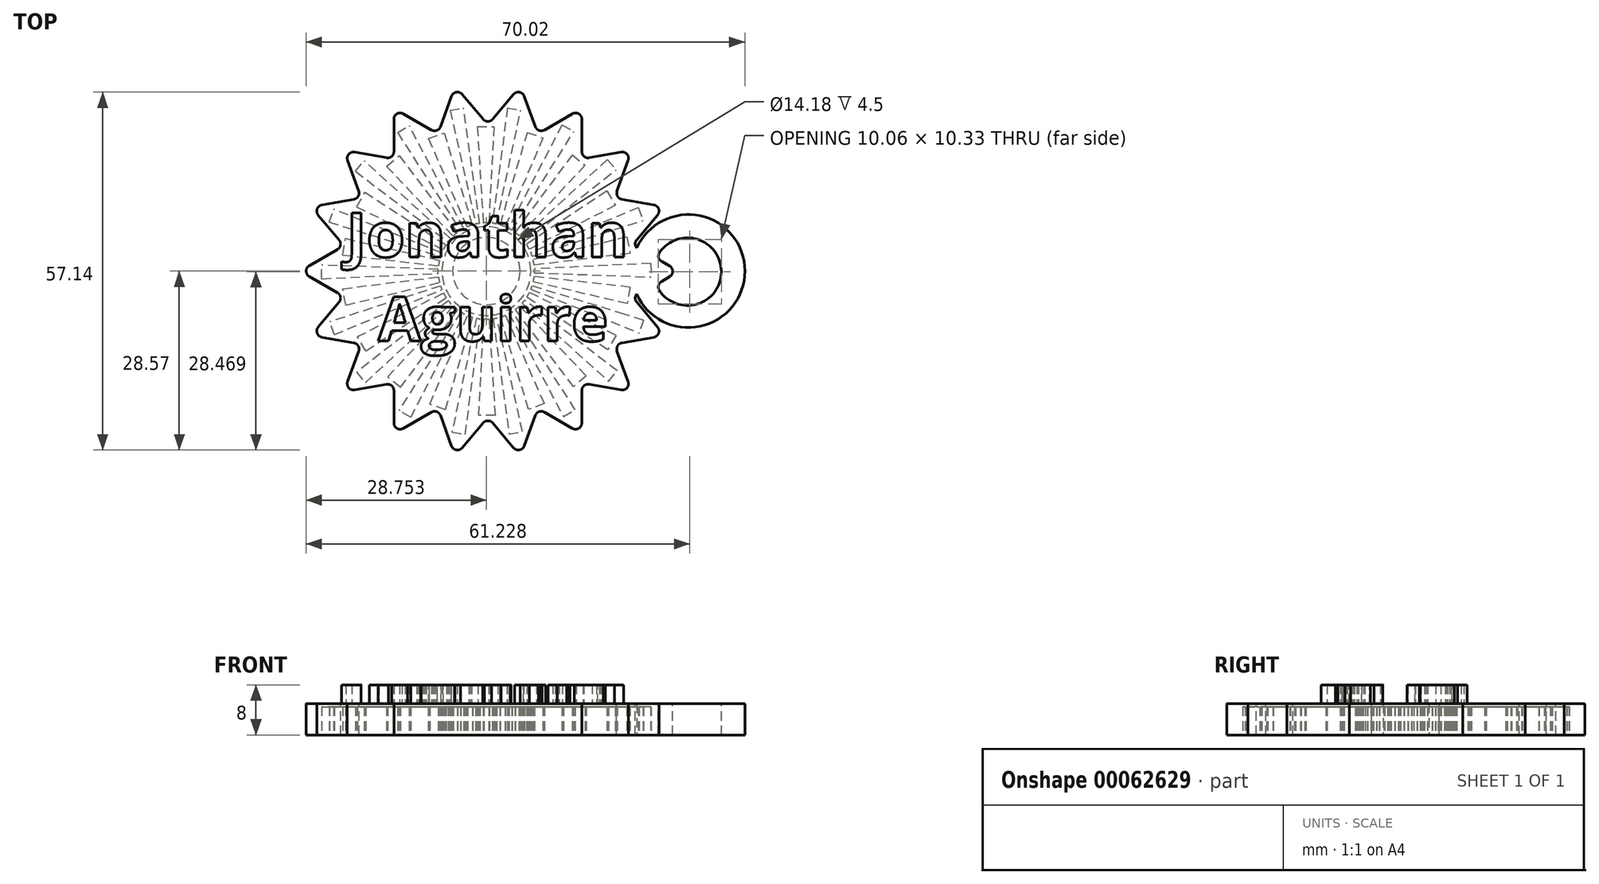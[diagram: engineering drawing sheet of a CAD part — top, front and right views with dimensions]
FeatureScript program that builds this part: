
annotation { "Feature Type Name" : "Feature", "Feature Type Description" : "" }
export const myFeature = defineFeature(function(context is Context, id is Id, definition is map)
    precondition{}
    {
        {
            var Q0;
            Q0=qCreatedBy(makeId("Top.planeOp"),FACE);
            var sketch = newSketch(context, id + "F0", { "sketchPlane" : qUnion([Q0])});
            skLineSegment(sketch, "E0", {"start": v(-64.22, 4.05) * mm, "end": v(-69.43, 10.26) * mm});
            skLineSegment(sketch, "E1", {"start": v(-69.43, 10.26) * mm, "end": v(-61.45, 11.67) * mm});
            skCircle(sketch, "E2.0", {"center": v(-41.24, 0) * mm, "radius": 30 * mm, "construction": true});
            skLineSegment(sketch, "E3", {"start": v(-61.45, 11.67) * mm, "end": v(-64.22, 19.28) * mm});
            skLineSegment(sketch, "E4", {"start": v(-64.22, 19.28) * mm, "end": v(-56.24, 17.88) * mm});
            skLineSegment(sketch, "E5", {"start": v(-56.24, 17.88) * mm, "end": v(-56.24, 25.98) * mm});
            skLineSegment(sketch, "E6", {"start": v(-56.24, 25.98) * mm, "end": v(-49.22, 21.93) * mm});
            skLineSegment(sketch, "E7", {"start": v(-49.22, 21.93) * mm, "end": v(-46.45, 29.54) * mm});
            skLineSegment(sketch, "E8", {"start": v(-46.45, 29.54) * mm, "end": v(-41.24, 23.34) * mm});
            skLineSegment(sketch, "E9", {"start": v(-41.24, 23.34) * mm, "end": v(-36.03, 29.54) * mm});
            skLineSegment(sketch, "E10", {"start": v(-36.03, 29.54) * mm, "end": v(-33.26, 21.93) * mm});
            skLineSegment(sketch, "E11", {"start": v(-33.26, 21.93) * mm, "end": v(-26.24, 25.98) * mm});
            skLineSegment(sketch, "E12", {"start": v(-26.24, 25.98) * mm, "end": v(-26.24, 17.88) * mm});
            skLineSegment(sketch, "E13", {"start": v(-26.24, 17.88) * mm, "end": v(-18.26, 19.28) * mm});
            skLineSegment(sketch, "E14", {"start": v(-18.26, 19.28) * mm, "end": v(-21.03, 11.67) * mm});
            skLineSegment(sketch, "E15", {"start": v(-21.03, 11.67) * mm, "end": v(-13.05, 10.26) * mm});
            skLineSegment(sketch, "E16", {"start": v(-13.05, 10.26) * mm, "end": v(-18.26, 4.05) * mm});
            skLineSegment(sketch, "E17", {"start": v(-18.26, 4.05) * mm, "end": v(-11.24, 0) * mm});
            skLineSegment(sketch, "E18", {"start": v(-11.24, 0) * mm, "end": v(-18.26, -4.05) * mm});
            skLineSegment(sketch, "E19", {"start": v(-18.26, -4.05) * mm, "end": v(-13.05, -10.26) * mm});
            skLineSegment(sketch, "E20", {"start": v(-13.05, -10.26) * mm, "end": v(-21.03, -11.67) * mm});
            skLineSegment(sketch, "E21", {"start": v(-21.03, -11.67) * mm, "end": v(-18.26, -19.28) * mm});
            skLineSegment(sketch, "E22", {"start": v(-18.26, -19.28) * mm, "end": v(-26.24, -17.88) * mm});
            skLineSegment(sketch, "E23", {"start": v(-26.24, -17.88) * mm, "end": v(-26.24, -25.98) * mm});
            skLineSegment(sketch, "E24", {"start": v(-26.24, -25.98) * mm, "end": v(-33.26, -21.93) * mm});
            skLineSegment(sketch, "E25", {"start": v(-33.26, -21.93) * mm, "end": v(-36.03, -29.54) * mm});
            skLineSegment(sketch, "E26", {"start": v(-46.45, -29.54) * mm, "end": v(-49.22, -21.93) * mm});
            skLineSegment(sketch, "E27", {"start": v(-49.22, -21.93) * mm, "end": v(-56.24, -25.98) * mm});
            skLineSegment(sketch, "E28", {"start": v(-56.24, -25.98) * mm, "end": v(-56.24, -17.88) * mm});
            skLineSegment(sketch, "E29", {"start": v(-56.24, -17.88) * mm, "end": v(-64.22, -19.28) * mm});
            skLineSegment(sketch, "E30", {"start": v(-64.22, -19.28) * mm, "end": v(-61.45, -11.67) * mm});
            skLineSegment(sketch, "E31", {"start": v(-61.45, -11.67) * mm, "end": v(-69.43, -10.26) * mm});
            skLineSegment(sketch, "E32", {"start": v(-69.43, -10.26) * mm, "end": v(-64.22, -4.05) * mm});
            skLineSegment(sketch, "E33", {"start": v(-64.22, -4.05) * mm, "end": v(-71.24, 0) * mm});
            skLineSegment(sketch, "E34", {"start": v(-71.24, 0) * mm, "end": v(-64.22, 4.05) * mm});
            skLineSegment(sketch, "E35", {"start": v(-46.45, -29.54) * mm, "end": v(-41.24, -23.34) * mm});
            skLineSegment(sketch, "E36", {"start": v(-41.24, -23.34) * mm, "end": v(-36.03, -29.54) * mm});
            skSolve(sketch);
        }
        {
            var Q0;
            Q0=qSketchRegion(id+"F0",true);
            extrude(context, id + "F1", {"entities" : qUnion([Q0]), "depth" : 5 * mm});
        }
        {
            var Q0;
            Q0=makeQuery(id+"F1.opExtrude","SWEPT_EDGE",EDGE,{"disambiguationData":[OSD([sQuery(id+"F0.wireOp",EDGE,"E26"),sQuery(id+"F0.wireOp",EDGE,"E27")])]});
            var Q1;
            Q1=makeQuery(id+"F1.opExtrude","SWEPT_EDGE",EDGE,{"disambiguationData":[OSD([sQuery(id+"F0.wireOp",EDGE,"E28"),sQuery(id+"F0.wireOp",EDGE,"E29")])]});
            var Q2;
            Q2=makeQuery(id+"F1.opExtrude","SWEPT_EDGE",EDGE,{"disambiguationData":[OSD([sQuery(id+"F0.wireOp",EDGE,"E30"),sQuery(id+"F0.wireOp",EDGE,"E31")])]});
            var Q3;
            Q3=makeQuery(id+"F1.opExtrude","SWEPT_EDGE",EDGE,{"disambiguationData":[OSD([sQuery(id+"F0.wireOp",EDGE,"E32"),sQuery(id+"F0.wireOp",EDGE,"E33")])]});
            var Q4;
            Q4=makeQuery(id+"F1.opExtrude","SWEPT_EDGE",EDGE,{"disambiguationData":[OSD([sQuery(id+"F0.wireOp",EDGE,"E0"),sQuery(id+"F0.wireOp",EDGE,"E34")])]});
            var Q5;
            Q5=makeQuery(id+"F1.opExtrude","SWEPT_EDGE",EDGE,{"disambiguationData":[OSD([sQuery(id+"F0.wireOp",EDGE,"E1"),sQuery(id+"F0.wireOp",EDGE,"E3")])]});
            var Q6;
            Q6=makeQuery(id+"F1.opExtrude","SWEPT_EDGE",EDGE,{"disambiguationData":[OSD([sQuery(id+"F0.wireOp",EDGE,"E4"),sQuery(id+"F0.wireOp",EDGE,"E5")])]});
            var Q7;
            Q7=makeQuery(id+"F1.opExtrude","SWEPT_EDGE",EDGE,{"disambiguationData":[OSD([sQuery(id+"F0.wireOp",EDGE,"E6"),sQuery(id+"F0.wireOp",EDGE,"E7")])]});
            var Q8;
            Q8=makeQuery(id+"F1.opExtrude","SWEPT_EDGE",EDGE,{"disambiguationData":[OSD([sQuery(id+"F0.wireOp",EDGE,"E8"),sQuery(id+"F0.wireOp",EDGE,"E9")])]});
            var Q9;
            Q9=makeQuery(id+"F1.opExtrude","SWEPT_EDGE",EDGE,{"disambiguationData":[OSD([sQuery(id+"F0.wireOp",EDGE,"E10"),sQuery(id+"F0.wireOp",EDGE,"E11")])]});
            var Q10;
            Q10=makeQuery(id+"F1.opExtrude","SWEPT_EDGE",EDGE,{"disambiguationData":[OSD([sQuery(id+"F0.wireOp",EDGE,"E35"),sQuery(id+"F0.wireOp",EDGE,"E36")])]});
            var Q11;
            Q11=makeQuery(id+"F1.opExtrude","SWEPT_EDGE",EDGE,{"disambiguationData":[OSD([sQuery(id+"F0.wireOp",EDGE,"E24"),sQuery(id+"F0.wireOp",EDGE,"E25")])]});
            var Q12;
            Q12=makeQuery(id+"F1.opExtrude","SWEPT_EDGE",EDGE,{"disambiguationData":[OSD([sQuery(id+"F0.wireOp",EDGE,"E22"),sQuery(id+"F0.wireOp",EDGE,"E23")])]});
            var Q13;
            Q13=makeQuery(id+"F1.opExtrude","SWEPT_EDGE",EDGE,{"disambiguationData":[OSD([sQuery(id+"F0.wireOp",EDGE,"E20"),sQuery(id+"F0.wireOp",EDGE,"E21")])]});
            var Q14;
            Q14=makeQuery(id+"F1.opExtrude","SWEPT_EDGE",EDGE,{"disambiguationData":[OSD([sQuery(id+"F0.wireOp",EDGE,"E12"),sQuery(id+"F0.wireOp",EDGE,"E13")])]});
            var Q15;
            Q15=makeQuery(id+"F1.opExtrude","SWEPT_EDGE",EDGE,{"disambiguationData":[OSD([sQuery(id+"F0.wireOp",EDGE,"E14"),sQuery(id+"F0.wireOp",EDGE,"E15")])]});
            var Q16;
            Q16=makeQuery(id+"F1.opExtrude","SWEPT_EDGE",EDGE,{"disambiguationData":[OSD([sQuery(id+"F0.wireOp",EDGE,"E16"),sQuery(id+"F0.wireOp",EDGE,"E17")])]});
            var Q17;
            Q17=makeQuery(id+"F1.opExtrude","SWEPT_EDGE",EDGE,{"disambiguationData":[OSD([sQuery(id+"F0.wireOp",EDGE,"E18"),sQuery(id+"F0.wireOp",EDGE,"E19")])]});
            fillet(context, id + "F2", {"entities" : qUnion([Q0, Q1, Q2, Q3, Q4, Q5, Q6, Q7, Q8, Q9, Q10, Q11, Q12, Q13, Q14, Q15, Q16, Q17]), "radius" : 1 * mm, "tangentPropagation" : true, "allowEdgeOverflow" : false});
        }
        {
            var Q0;
            Q0=makeQuery(id+"F1.opExtrude","SWEPT_EDGE",EDGE,{"disambiguationData":[OSD([sQuery(id+"F0.wireOp",EDGE,"E9"),sQuery(id+"F0.wireOp",EDGE,"E10")])]});
            var Q1;
            Q1=makeQuery(id+"F1.opExtrude","SWEPT_EDGE",EDGE,{"disambiguationData":[OSD([sQuery(id+"F0.wireOp",EDGE,"E11"),sQuery(id+"F0.wireOp",EDGE,"E12")])]});
            var Q2;
            Q2=makeQuery(id+"F1.opExtrude","SWEPT_EDGE",EDGE,{"disambiguationData":[OSD([sQuery(id+"F0.wireOp",EDGE,"E13"),sQuery(id+"F0.wireOp",EDGE,"E14")])]});
            var Q3;
            Q3=makeQuery(id+"F1.opExtrude","SWEPT_EDGE",EDGE,{"disambiguationData":[OSD([sQuery(id+"F0.wireOp",EDGE,"E15"),sQuery(id+"F0.wireOp",EDGE,"E16")])]});
            var Q4;
            Q4=makeQuery(id+"F1.opExtrude","SWEPT_EDGE",EDGE,{"disambiguationData":[OSD([sQuery(id+"F0.wireOp",EDGE,"E17"),sQuery(id+"F0.wireOp",EDGE,"E18")])]});
            var Q5;
            Q5=makeQuery(id+"F1.opExtrude","SWEPT_EDGE",EDGE,{"disambiguationData":[OSD([sQuery(id+"F0.wireOp",EDGE,"E19"),sQuery(id+"F0.wireOp",EDGE,"E20")])]});
            var Q6;
            Q6=makeQuery(id+"F1.opExtrude","SWEPT_EDGE",EDGE,{"disambiguationData":[OSD([sQuery(id+"F0.wireOp",EDGE,"E5"),sQuery(id+"F0.wireOp",EDGE,"E6")])]});
            var Q7;
            Q7=makeQuery(id+"F1.opExtrude","SWEPT_EDGE",EDGE,{"disambiguationData":[OSD([sQuery(id+"F0.wireOp",EDGE,"E7"),sQuery(id+"F0.wireOp",EDGE,"E8")])]});
            var Q8;
            Q8=makeQuery(id+"F1.opExtrude","SWEPT_EDGE",EDGE,{"disambiguationData":[OSD([sQuery(id+"F0.wireOp",EDGE,"E3"),sQuery(id+"F0.wireOp",EDGE,"E4")])]});
            var Q9;
            Q9=makeQuery(id+"F1.opExtrude","SWEPT_EDGE",EDGE,{"disambiguationData":[OSD([sQuery(id+"F0.wireOp",EDGE,"E0"),sQuery(id+"F0.wireOp",EDGE,"E1")])]});
            var Q10;
            Q10=makeQuery(id+"F1.opExtrude","SWEPT_EDGE",EDGE,{"disambiguationData":[OSD([sQuery(id+"F0.wireOp",EDGE,"E33"),sQuery(id+"F0.wireOp",EDGE,"E34")])]});
            var Q11;
            Q11=makeQuery(id+"F1.opExtrude","SWEPT_EDGE",EDGE,{"disambiguationData":[OSD([sQuery(id+"F0.wireOp",EDGE,"E31"),sQuery(id+"F0.wireOp",EDGE,"E32")])]});
            var Q12;
            Q12=makeQuery(id+"F1.opExtrude","SWEPT_EDGE",EDGE,{"disambiguationData":[OSD([sQuery(id+"F0.wireOp",EDGE,"E29"),sQuery(id+"F0.wireOp",EDGE,"E30")])]});
            var Q13;
            Q13=makeQuery(id+"F1.opExtrude","SWEPT_EDGE",EDGE,{"disambiguationData":[OSD([sQuery(id+"F0.wireOp",EDGE,"E27"),sQuery(id+"F0.wireOp",EDGE,"E28")])]});
            var Q14;
            Q14=makeQuery(id+"F1.opExtrude","SWEPT_EDGE",EDGE,{"disambiguationData":[OSD([sQuery(id+"F0.wireOp",EDGE,"E26"),sQuery(id+"F0.wireOp",EDGE,"E35")])]});
            var Q15;
            Q15=makeQuery(id+"F1.opExtrude","SWEPT_EDGE",EDGE,{"disambiguationData":[OSD([sQuery(id+"F0.wireOp",EDGE,"E25"),sQuery(id+"F0.wireOp",EDGE,"E36")])]});
            var Q16;
            Q16=makeQuery(id+"F1.opExtrude","SWEPT_EDGE",EDGE,{"disambiguationData":[OSD([sQuery(id+"F0.wireOp",EDGE,"E23"),sQuery(id+"F0.wireOp",EDGE,"E24")])]});
            var Q17;
            Q17=makeQuery(id+"F1.opExtrude","SWEPT_EDGE",EDGE,{"disambiguationData":[OSD([sQuery(id+"F0.wireOp",EDGE,"E21"),sQuery(id+"F0.wireOp",EDGE,"E22")])]});
            fillet(context, id + "F3", {"entities" : qUnion([Q0, Q1, Q2, Q3, Q4, Q5, Q6, Q7, Q8, Q9, Q10, Q11, Q12, Q13, Q14, Q15, Q16, Q17]), "radius" : 1 * mm, "tangentPropagation" : true, "allowEdgeOverflow" : false});
        }
        {
            var Q0;
            Q0=qCreatedBy(makeId("Top.planeOp"),FACE);
            var sketch = newSketch(context, id + "F4", { "sketchPlane" : qUnion([Q0])});
            skCircle(sketch, "E37", {"center": v(-9.24, 0) * mm, "radius": 9.02 * mm});
            skSolve(sketch);
        }
        {
            var Q0;
            Q0=qSketchRegion(id+"F4",true);
            var Q1;
            {var subQ0=sQuery(id+"F0.wireOp",EDGE,"E30");var subQ1=sQuery(id+"F0.wireOp",EDGE,"E16");var subQ2=sQuery(id+"F0.wireOp",EDGE,"E31");var subQ3=sQuery(id+"F0.wireOp",EDGE,"E27");var subQ4=sQuery(id+"F0.wireOp",EDGE,"E23");var subQ5=sQuery(id+"F0.wireOp",EDGE,"E21");var subQ6=sQuery(id+"F0.wireOp",EDGE,"E13");var subQ7=sQuery(id+"F0.wireOp",EDGE,"E14");var subQ8=sQuery(id+"F0.wireOp",EDGE,"E20");var subQ9=sQuery(id+"F0.wireOp",EDGE,"E22");var subQ10=sQuery(id+"F0.wireOp",EDGE,"E19");var subQ11=sQuery(id+"F0.wireOp",EDGE,"E11");var subQ12=sQuery(id+"F0.wireOp",EDGE,"E18");var subQ13=sQuery(id+"F0.wireOp",EDGE,"E17");var subQ14=sQuery(id+"F0.wireOp",EDGE,"E12");var subQ15=sQuery(id+"F0.wireOp",EDGE,"E4");var subQ16=sQuery(id+"F0.wireOp",EDGE,"E3");var subQ17=sQuery(id+"F0.wireOp",EDGE,"E32");var subQ18=sQuery(id+"F0.wireOp",EDGE,"E1");var subQ19=sQuery(id+"F0.wireOp",EDGE,"E9");var subQ20=sQuery(id+"F0.wireOp",EDGE,"E0");var subQ21=sQuery(id+"F0.wireOp",EDGE,"E5");var subQ22=sQuery(id+"F0.wireOp",EDGE,"E6");var subQ23=sQuery(id+"F0.wireOp",EDGE,"E7");var subQ24=sQuery(id+"F0.wireOp",EDGE,"E36");var subQ25=sQuery(id+"F0.wireOp",EDGE,"E15");var subQ26=sQuery(id+"F0.wireOp",EDGE,"E8");var subQ27=sQuery(id+"F0.wireOp",EDGE,"E34");var subQ28=sQuery(id+"F0.wireOp",EDGE,"E25");var subQ29=sQuery(id+"F0.wireOp",EDGE,"E29");var subQ30=sQuery(id+"F0.wireOp",EDGE,"E26");var subQ31=sQuery(id+"F0.wireOp",EDGE,"E35");var subQ32=sQuery(id+"F0.wireOp",EDGE,"E33");var subQ33=sQuery(id+"F0.wireOp",EDGE,"E24");var subQ34=sQuery(id+"F0.wireOp",EDGE,"E10");var subQ35=sQuery(id+"F0.wireOp",EDGE,"E28");Q1=makeQuery(id+"FIdaEZY0NoQjCEp_1.boolean.opBoolean","SPLIT",FACE,{"disambiguationData":[TD([makeQuery(id+"F1.opExtrude","SWEPT_FACE",FACE,{"disambiguationData":[OSD([subQ20])]})])],"derivedFrom":makeQuery(id+"F1.opExtrude","CAP_FACE",FACE,{"disambiguationData":[OSD([subQ20,subQ18,subQ16,subQ15,subQ21,subQ22,subQ23,subQ26,subQ19,subQ34,subQ11,subQ14,subQ6,subQ7,subQ25,subQ1,subQ13,subQ12,subQ10,subQ8,subQ5,subQ9,subQ4,subQ33,subQ28,subQ30,subQ3,subQ35,subQ29,subQ0,subQ2,subQ17,subQ32,subQ27,subQ31,subQ24])],"isStart":false})});}
            extrude(context, id + "F5", {"entities" : qUnion([Q0]), "operationType" : NewBodyOperationType.ADD, "endBound" : BoundingType.UP_TO_SURFACE, "endBoundEntityFace" : qUnion([Q1]), "depth" : 25 * mm});
        }
        {
            var Q0;
            {var subQ0=sQuery(id+"F0.wireOp",EDGE,"E36");var subQ1=sQuery(id+"F0.wireOp",EDGE,"E35");var subQ2=sQuery(id+"F0.wireOp",EDGE,"E34");var subQ3=sQuery(id+"F0.wireOp",EDGE,"E33");var subQ4=sQuery(id+"F0.wireOp",EDGE,"E32");var subQ5=sQuery(id+"F0.wireOp",EDGE,"E31");var subQ6=sQuery(id+"F0.wireOp",EDGE,"E30");var subQ7=sQuery(id+"F0.wireOp",EDGE,"E29");var subQ8=sQuery(id+"F0.wireOp",EDGE,"E28");var subQ9=sQuery(id+"F0.wireOp",EDGE,"E27");var subQ10=sQuery(id+"F0.wireOp",EDGE,"E26");var subQ11=sQuery(id+"F0.wireOp",EDGE,"E25");var subQ12=sQuery(id+"F0.wireOp",EDGE,"E24");var subQ13=sQuery(id+"F0.wireOp",EDGE,"E23");var subQ14=sQuery(id+"F0.wireOp",EDGE,"E22");var subQ15=sQuery(id+"F0.wireOp",EDGE,"E21");var subQ16=sQuery(id+"F0.wireOp",EDGE,"E20");var subQ17=sQuery(id+"F0.wireOp",EDGE,"E19");var subQ18=sQuery(id+"F0.wireOp",EDGE,"E18");var subQ19=sQuery(id+"F0.wireOp",EDGE,"E17");var subQ20=sQuery(id+"F0.wireOp",EDGE,"E16");var subQ21=sQuery(id+"F0.wireOp",EDGE,"E15");var subQ22=sQuery(id+"F0.wireOp",EDGE,"E14");var subQ23=sQuery(id+"F0.wireOp",EDGE,"E13");var subQ24=sQuery(id+"F0.wireOp",EDGE,"E12");var subQ25=sQuery(id+"F0.wireOp",EDGE,"E11");var subQ26=sQuery(id+"F0.wireOp",EDGE,"E10");var subQ27=sQuery(id+"F0.wireOp",EDGE,"E9");var subQ28=sQuery(id+"F0.wireOp",EDGE,"E8");var subQ29=sQuery(id+"F0.wireOp",EDGE,"E7");var subQ30=sQuery(id+"F0.wireOp",EDGE,"E6");var subQ31=sQuery(id+"F0.wireOp",EDGE,"E5");var subQ32=sQuery(id+"F0.wireOp",EDGE,"E4");var subQ33=sQuery(id+"F0.wireOp",EDGE,"E3");var subQ34=sQuery(id+"F0.wireOp",EDGE,"E1");var subQ35=sQuery(id+"F0.wireOp",EDGE,"E0");Q0=makeQuery(id+"F5.boolean.opBoolean","MERGE",FACE,{"derivedFrom":[makeQuery(id+"F1.opExtrude","CAP_FACE",FACE,{"disambiguationData":[OSD([subQ35,subQ34,subQ33,subQ32,subQ31,subQ30,subQ29,subQ28,subQ27,subQ26,subQ25,subQ24,subQ23,subQ22,subQ21,subQ20,subQ19,subQ18,subQ17,subQ16,subQ15,subQ14,subQ13,subQ12,subQ11,subQ10,subQ9,subQ8,subQ7,subQ6,subQ5,subQ4,subQ3,subQ2,subQ1,subQ0])],"isStart":false}),makeQuery(id+"F5.opExtrude","CAP_FACE",FACE,{"disambiguationData":[OSD([subQ35,subQ34,subQ33,subQ32,subQ31,subQ30,subQ29,subQ28,subQ27,subQ26,subQ25,subQ24,subQ23,subQ22,subQ21,subQ20,subQ19,subQ18,subQ17,subQ16,subQ15,subQ14,subQ13,subQ12,subQ11,subQ10,subQ9,subQ8,subQ7,subQ6,subQ5,subQ4,subQ3,subQ2,subQ1,subQ0])],"isStart":false})]});}
            var sketch = newSketch(context, id + "F6", { "sketchPlane" : qUnion([Q0])});
            skLineSegment(sketch, "E38", {"start": v(-14.37, 2) * mm, "end": v(-10.75, 0) * mm});
            skLineSegment(sketch, "E39", {"start": v(-10.75, 0) * mm, "end": v(-14.37, -2.19) * mm});
            skArc(sketch, "E40", {"start": v(-14.37, -2.19) * mm, "mid": v(-3.98, -0.1) * mm, "end": v(-14.37, 2) * mm});
            skSolve(sketch);
        }
        {
            var Q0;
            Q0=qSketchRegion(id+"F6",true);
            var Q1;
            Q1=makeQuery(id+"F5.boolean.opBoolean","MERGE",FACE,{"derivedFrom":[makeQuery(id+"F1.opExtrude","CAP_FACE",FACE,{"disambiguationData":[OSD([sQuery(id+"F0.wireOp",EDGE,"E0"),sQuery(id+"F0.wireOp",EDGE,"E1"),sQuery(id+"F0.wireOp",EDGE,"E3"),sQuery(id+"F0.wireOp",EDGE,"E4"),sQuery(id+"F0.wireOp",EDGE,"E5"),sQuery(id+"F0.wireOp",EDGE,"E6"),sQuery(id+"F0.wireOp",EDGE,"E7"),sQuery(id+"F0.wireOp",EDGE,"E8"),sQuery(id+"F0.wireOp",EDGE,"E9"),sQuery(id+"F0.wireOp",EDGE,"E10"),sQuery(id+"F0.wireOp",EDGE,"E11"),sQuery(id+"F0.wireOp",EDGE,"E12"),sQuery(id+"F0.wireOp",EDGE,"E13"),sQuery(id+"F0.wireOp",EDGE,"E14"),sQuery(id+"F0.wireOp",EDGE,"E15"),sQuery(id+"F0.wireOp",EDGE,"E16"),sQuery(id+"F0.wireOp",EDGE,"E17"),sQuery(id+"F0.wireOp",EDGE,"E18"),sQuery(id+"F0.wireOp",EDGE,"E19"),sQuery(id+"F0.wireOp",EDGE,"E20"),sQuery(id+"F0.wireOp",EDGE,"E21"),sQuery(id+"F0.wireOp",EDGE,"E22"),sQuery(id+"F0.wireOp",EDGE,"E23"),sQuery(id+"F0.wireOp",EDGE,"E24"),sQuery(id+"F0.wireOp",EDGE,"E25"),sQuery(id+"F0.wireOp",EDGE,"E26"),sQuery(id+"F0.wireOp",EDGE,"E27"),sQuery(id+"F0.wireOp",EDGE,"E28"),sQuery(id+"F0.wireOp",EDGE,"E29"),sQuery(id+"F0.wireOp",EDGE,"E30"),sQuery(id+"F0.wireOp",EDGE,"E31"),sQuery(id+"F0.wireOp",EDGE,"E32"),sQuery(id+"F0.wireOp",EDGE,"E33"),sQuery(id+"F0.wireOp",EDGE,"E34"),sQuery(id+"F0.wireOp",EDGE,"E35"),sQuery(id+"F0.wireOp",EDGE,"E36")])],"isStart":true}),makeQuery(id+"F5.opExtrude","CAP_FACE",FACE,{"disambiguationData":[OSD([sQuery(id+"F4.wireOp",EDGE,"E37")])],"isStart":true})]});
            extrude(context, id + "F7", {"entities" : qUnion([Q0]), "operationType" : NewBodyOperationType.REMOVE, "endBound" : BoundingType.UP_TO_SURFACE, "oppositeDirection" : true, "endBoundEntityFace" : qUnion([Q1]), "depth" : 25 * mm});
        }
        {
            var Q0;
            Q0=makeQuery(id+"F7.boolean.opBoolean","COPY",EDGE,{"derivedFrom":makeQuery(id+"F7.opExtrude","SWEPT_EDGE",EDGE,{"disambiguationData":[OSD([sQuery(id+"F6.wireOp",EDGE,"KMGjyx1H-Efwy-Ger7-KHIj-FZDtgPy88TKw"),sQuery(id+"F6.wireOp",EDGE,"Em1Z4o3I-NRpS-VtHU-MFej-VVcVSapDzxZl")])]})});
            var Q1;
            Q1=makeQuery(id+"F7.boolean.opBoolean","COPY",EDGE,{"derivedFrom":makeQuery(id+"F7.opExtrude","SWEPT_EDGE",EDGE,{"disambiguationData":[OSD([sQuery(id+"F6.wireOp",EDGE,"E38"),sQuery(id+"F6.wireOp",EDGE,"E39")])]})});
            var Q2;
            Q2=makeQuery(id+"F7.boolean.opBoolean","COPY",EDGE,{"derivedFrom":makeQuery(id+"F7.opExtrude","SWEPT_EDGE",EDGE,{"disambiguationData":[OSD([sQuery(id+"F6.wireOp",EDGE,"E39"),sQuery(id+"F6.wireOp",EDGE,"E40")])]})});
            var Q3;
            Q3=makeQuery(id+"F7.boolean.opBoolean","COPY",EDGE,{"derivedFrom":makeQuery(id+"F7.opExtrude","SWEPT_EDGE",EDGE,{"disambiguationData":[OSD([sQuery(id+"F6.wireOp",EDGE,"E38"),sQuery(id+"F6.wireOp",EDGE,"E40")])]})});
            fillet(context, id + "F8", {"entities" : qUnion([Q0, Q1, Q2, Q3]), "radius" : 1 * mm, "tangentPropagation" : true, "allowEdgeOverflow" : false});
        }
        {
            var Q0;
            Q0=makeQuery(id+"F0.imprint","IMPRINT",FACE,{"disambiguationData":[TD([[makeQuery(id+"F0.imprint","IMPRINT",EDGE,{"derivedFrom":sQuery(id+"F0.wireOp",EDGE,"E0")}),-1.0]])]});
            var sketch = newSketch(context, id + "F9", { "sketchPlane" : qUnion([Q0])});
            skCircle(sketch, "E41", {"center": v(-41.49, 0) * mm, "radius": 26.28 * mm, "construction": true});
            skCircle(sketch, "E42", {"center": v(-41.49, 0) * mm, "radius": 23.08 * mm, "construction": true});
            skLineSegment(sketch, "E43", {"start": v(-41.49, 0) * mm, "end": v(-21.98, -17.6) * mm, "construction": true});
            skLineSegment(sketch, "E44", {"start": v(-21.98, -17.6) * mm, "end": v(-20.6, -15.94) * mm, "construction": true});
            skLineSegment(sketch, "E45", {"start": v(-20.6, -15.94) * mm, "end": v(-41.49, 0) * mm, "construction": true});
            skLineSegment(sketch, "E46", {"start": v(-41.49, 0) * mm, "end": v(-22.13, -12.57) * mm, "construction": true});
            skLineSegment(sketch, "E47", {"start": v(-22.13, -12.57) * mm, "end": v(-20.8, -10.26) * mm, "construction": true});
            skLineSegment(sketch, "E48", {"start": v(-20.8, -10.26) * mm, "end": v(-41.49, 0) * mm, "construction": true});
            skLineSegment(sketch, "E49", {"start": v(-41.49, 0) * mm, "end": v(-21.03, -11.67) * mm, "construction": true});
            skLineSegment(sketch, "E50", {"start": v(-41.49, 0) * mm, "end": v(-18.26, -19.28) * mm, "construction": true});
            skLineSegment(sketch, "E51", {"start": v(-20.8, -10.26) * mm, "end": v(-21.03, -11.67) * mm, "construction": true});
            skLineSegment(sketch, "E52", {"start": v(-22.13, -12.57) * mm, "end": v(-21.03, -11.67) * mm, "construction": true});
            skLineSegment(sketch, "E53", {"start": v(-18.26, -19.28) * mm, "end": v(-21.98, -17.6) * mm, "construction": true});
            skLineSegment(sketch, "E54", {"start": v(-20.6, -15.94) * mm, "end": v(-18.26, -19.28) * mm, "construction": true});
            skLineSegment(sketch, "E55", {"start": v(-35.78, -5.15) * mm, "end": v(-21.98, -17.6) * mm});
            skLineSegment(sketch, "E56", {"start": v(-20.6, -15.94) * mm, "end": v(-35.38, -4.66) * mm});
            skLineSegment(sketch, "E57", {"start": v(-22.13, -12.57) * mm, "end": v(-35.04, -4.18) * mm});
            skLineSegment(sketch, "E58", {"start": v(-20.8, -10.26) * mm, "end": v(-22.13, -12.57) * mm});
            skLineSegment(sketch, "E59", {"start": v(-20.8, -10.26) * mm, "end": v(-34.6, -3.42) * mm});
            skLineSegment(sketch, "E60.1.0", {"start": v(-34.37, -2.89) * mm, "end": v(-17.13, -9.87) * mm});
            skLineSegment(sketch, "E60.1.1", {"start": v(-17.13, -9.87) * mm, "end": v(-16.4, -7.83) * mm, "construction": true});
            skLineSegment(sketch, "E60.1.2", {"start": v(-16.4, -7.83) * mm, "end": v(-19.45, -6.88) * mm});
            skLineSegment(sketch, "E60.1.3", {"start": v(-19, -5.2) * mm, "end": v(-34, -1.73) * mm});
            skLineSegment(sketch, "E60.1.4", {"start": v(-18.55, -2.57) * mm, "end": v(-19, -5.2) * mm});
            skLineSegment(sketch, "E60.1.5", {"start": v(-18.55, -2.57) * mm, "end": v(-33.85, -0.86) * mm});
            skLineSegment(sketch, "E60.2.0", {"start": v(-33.8, -0.28) * mm, "end": v(-15.22, -0.95) * mm});
            skLineSegment(sketch, "E60.2.1", {"start": v(-15.22, -0.95) * mm, "end": v(-15.23, 1.22) * mm, "construction": true});
            skLineSegment(sketch, "E60.2.2", {"start": v(-15.23, 1.22) * mm, "end": v(-33.81, 0.36) * mm});
            skLineSegment(sketch, "E60.2.3", {"start": v(-18.57, 2.81) * mm, "end": v(-33.86, 0.94) * mm});
            skLineSegment(sketch, "E60.2.4", {"start": v(-19.05, 5.43) * mm, "end": v(-18.57, 2.81) * mm});
            skLineSegment(sketch, "E60.2.5", {"start": v(-19.05, 5.43) * mm, "end": v(-34.02, 1.8) * mm});
            skLineSegment(sketch, "E60.3.0", {"start": v(-34.18, 2.37) * mm, "end": v(-16.48, 8.1) * mm});
            skLineSegment(sketch, "E60.3.1", {"start": v(-16.48, 8.1) * mm, "end": v(-17.23, 10.13) * mm, "construction": true});
            skLineSegment(sketch, "E60.3.2", {"start": v(-17.23, 10.13) * mm, "end": v(-34.4, 2.96) * mm});
            skLineSegment(sketch, "E60.3.3", {"start": v(-20.92, 10.48) * mm, "end": v(-34.64, 3.49) * mm});
            skLineSegment(sketch, "E60.3.4", {"start": v(-22.26, 12.78) * mm, "end": v(-20.92, 10.48) * mm});
            skLineSegment(sketch, "E60.3.5", {"start": v(-22.26, 12.78) * mm, "end": v(-35.09, 4.25) * mm});
            skLineSegment(sketch, "E60.4.0", {"start": v(-35.43, 4.72) * mm, "end": v(-20.76, 16.16) * mm});
            skLineSegment(sketch, "E60.4.1", {"start": v(-20.76, 16.16) * mm, "end": v(-22.16, 17.81) * mm, "construction": true});
            skLineSegment(sketch, "E60.4.2", {"start": v(-22.16, 17.81) * mm, "end": v(-35.84, 5.2) * mm});
            skLineSegment(sketch, "E60.4.3", {"start": v(-25.74, 16.88) * mm, "end": v(-36.25, 5.62) * mm});
            skLineSegment(sketch, "E60.4.4", {"start": v(-27.79, 18.58) * mm, "end": v(-25.74, 16.88) * mm});
            skLineSegment(sketch, "E60.4.5", {"start": v(-27.79, 18.58) * mm, "end": v(-36.93, 6.18) * mm});
            skLineSegment(sketch, "E60.5.0", {"start": v(-37.4, 6.51) * mm, "end": v(-27.53, 22.27) * mm});
            skLineSegment(sketch, "E60.5.1", {"start": v(-27.53, 22.27) * mm, "end": v(-29.42, 23.35) * mm, "construction": true});
            skLineSegment(sketch, "E60.5.2", {"start": v(-29.42, 23.35) * mm, "end": v(-37.96, 6.83) * mm});
            skLineSegment(sketch, "E60.5.3", {"start": v(-32.47, 21.25) * mm, "end": v(-38.48, 7.07) * mm});
            skLineSegment(sketch, "E60.5.4", {"start": v(-34.97, 22.15) * mm, "end": v(-32.47, 21.25) * mm});
            skLineSegment(sketch, "E60.5.5", {"start": v(-34.97, 22.15) * mm, "end": v(-39.32, 7.37) * mm});
            skLineSegment(sketch, "E60.6.0", {"start": v(-39.88, 7.51) * mm, "end": v(-36, 25.7) * mm});
            skLineSegment(sketch, "E60.6.1", {"start": v(-36, 25.7) * mm, "end": v(-38.13, 26.07) * mm, "construction": true});
            skLineSegment(sketch, "E60.6.2", {"start": v(-38.13, 26.07) * mm, "end": v(-40.5, 7.62) * mm});
            skLineSegment(sketch, "E60.6.3", {"start": v(-40.28, 23.05) * mm, "end": v(-41.08, 7.67) * mm});
            skLineSegment(sketch, "E60.6.4", {"start": v(-42.94, 23.04) * mm, "end": v(-40.28, 23.05) * mm});
            skLineSegment(sketch, "E60.6.5", {"start": v(-42.94, 23.04) * mm, "end": v(-41.97, 7.67) * mm});
            skLineSegment(sketch, "E60.7.0", {"start": v(-42.55, 7.6) * mm, "end": v(-45.11, 26.03) * mm});
            skLineSegment(sketch, "E60.7.1", {"start": v(-45.11, 26.03) * mm, "end": v(-47.25, 25.64) * mm, "construction": true});
            skLineSegment(sketch, "E60.7.2", {"start": v(-47.25, 25.64) * mm, "end": v(-43.17, 7.5) * mm});
            skLineSegment(sketch, "E60.7.3", {"start": v(-48.24, 22.08) * mm, "end": v(-43.73, 7.35) * mm});
            skLineSegment(sketch, "E60.7.4", {"start": v(-50.73, 21.15) * mm, "end": v(-48.24, 22.08) * mm});
            skLineSegment(sketch, "E60.7.5", {"start": v(-50.73, 21.15) * mm, "end": v(-44.56, 7.04) * mm});
            skLineSegment(sketch, "E60.8.0", {"start": v(-45.09, 6.79) * mm, "end": v(-53.8, 23.22) * mm});
            skLineSegment(sketch, "E60.8.1", {"start": v(-53.8, 23.22) * mm, "end": v(-55.67, 22.13) * mm, "construction": true});
            skLineSegment(sketch, "E60.8.2", {"start": v(-55.67, 22.13) * mm, "end": v(-45.63, 6.47) * mm});
            skLineSegment(sketch, "E60.8.3", {"start": v(-55.38, 18.44) * mm, "end": v(-46.11, 6.14) * mm});
            skLineSegment(sketch, "E60.8.4", {"start": v(-57.4, 16.72) * mm, "end": v(-55.38, 18.44) * mm});
            skLineSegment(sketch, "E60.8.5", {"start": v(-57.4, 16.72) * mm, "end": v(-46.79, 5.56) * mm});
            skLineSegment(sketch, "E60.9.0", {"start": v(-47.2, 5.15) * mm, "end": v(-61, 17.6) * mm});
            skLineSegment(sketch, "E60.9.1", {"start": v(-61, 17.6) * mm, "end": v(-62.38, 15.94) * mm, "construction": true});
            skLineSegment(sketch, "E60.9.2", {"start": v(-62.38, 15.94) * mm, "end": v(-47.6, 4.66) * mm});
            skLineSegment(sketch, "E60.9.3", {"start": v(-60.85, 12.57) * mm, "end": v(-47.93, 4.18) * mm});
            skLineSegment(sketch, "E60.9.4", {"start": v(-62.16, 10.26) * mm, "end": v(-60.85, 12.57) * mm});
            skLineSegment(sketch, "E60.9.5", {"start": v(-62.16, 10.26) * mm, "end": v(-48.37, 3.42) * mm});
            skLineSegment(sketch, "E60.10.0", {"start": v(-48.6, 2.89) * mm, "end": v(-65.84, 9.87) * mm});
            skLineSegment(sketch, "E60.10.1", {"start": v(-65.84, 9.87) * mm, "end": v(-66.57, 7.83) * mm, "construction": true});
            skLineSegment(sketch, "E60.10.2", {"start": v(-66.57, 7.83) * mm, "end": v(-48.82, 2.29) * mm});
            skLineSegment(sketch, "E60.10.3", {"start": v(-63.98, 5.2) * mm, "end": v(-48.97, 1.73) * mm});
            skLineSegment(sketch, "E60.10.4", {"start": v(-64.43, 2.57) * mm, "end": v(-63.98, 5.2) * mm});
            skLineSegment(sketch, "E60.10.5", {"start": v(-64.43, 2.57) * mm, "end": v(-49.12, 0.86) * mm});
            skLineSegment(sketch, "E60.11.0", {"start": v(-49.17, 0.28) * mm, "end": v(-67.75, 0.95) * mm});
            skLineSegment(sketch, "E60.11.1", {"start": v(-67.75, 0.95) * mm, "end": v(-67.74, -1.22) * mm, "construction": true});
            skLineSegment(sketch, "E60.11.2", {"start": v(-67.74, -1.22) * mm, "end": v(-49.16, -0.36) * mm});
            skLineSegment(sketch, "E60.11.3", {"start": v(-64.4, -2.81) * mm, "end": v(-49.11, -0.94) * mm});
            skLineSegment(sketch, "E60.11.4", {"start": v(-63.92, -5.43) * mm, "end": v(-64.4, -2.81) * mm});
            skLineSegment(sketch, "E60.11.5", {"start": v(-63.92, -5.43) * mm, "end": v(-48.95, -1.8) * mm});
            skLineSegment(sketch, "E60.12.0", {"start": v(-48.8, -2.37) * mm, "end": v(-66.5, -8.1) * mm});
            skLineSegment(sketch, "E60.12.1", {"start": v(-66.5, -8.1) * mm, "end": v(-65.74, -10.13) * mm, "construction": true});
            skLineSegment(sketch, "E60.12.2", {"start": v(-65.74, -10.13) * mm, "end": v(-48.58, -2.96) * mm});
            skLineSegment(sketch, "E60.12.3", {"start": v(-62.06, -10.48) * mm, "end": v(-48.33, -3.49) * mm});
            skLineSegment(sketch, "E60.12.4", {"start": v(-60.71, -12.78) * mm, "end": v(-62.06, -10.48) * mm});
            skLineSegment(sketch, "E60.12.5", {"start": v(-60.71, -12.78) * mm, "end": v(-47.89, -4.25) * mm});
            skLineSegment(sketch, "E60.13.0", {"start": v(-47.55, -4.72) * mm, "end": v(-62.22, -16.16) * mm});
            skLineSegment(sketch, "E60.13.1", {"start": v(-62.22, -16.16) * mm, "end": v(-60.81, -17.81) * mm, "construction": true});
            skLineSegment(sketch, "E60.13.2", {"start": v(-60.81, -17.81) * mm, "end": v(-47.14, -5.2) * mm});
            skLineSegment(sketch, "E60.13.3", {"start": v(-57.23, -16.88) * mm, "end": v(-46.73, -5.62) * mm});
            skLineSegment(sketch, "E60.13.4", {"start": v(-55.18, -18.58) * mm, "end": v(-57.23, -16.88) * mm});
            skLineSegment(sketch, "E60.13.5", {"start": v(-55.18, -18.58) * mm, "end": v(-46.05, -6.18) * mm});
            skLineSegment(sketch, "E60.14.0", {"start": v(-45.57, -6.51) * mm, "end": v(-55.44, -22.27) * mm});
            skLineSegment(sketch, "E60.14.1", {"start": v(-55.44, -22.27) * mm, "end": v(-53.56, -23.35) * mm, "construction": true});
            skLineSegment(sketch, "E60.14.2", {"start": v(-53.56, -23.35) * mm, "end": v(-45.01, -6.83) * mm});
            skLineSegment(sketch, "E60.14.3", {"start": v(-50.5, -21.25) * mm, "end": v(-44.49, -7.07) * mm});
            skLineSegment(sketch, "E60.14.4", {"start": v(-48, -22.15) * mm, "end": v(-50.5, -21.25) * mm});
            skLineSegment(sketch, "E60.14.5", {"start": v(-48, -22.15) * mm, "end": v(-43.66, -7.37) * mm});
            skLineSegment(sketch, "E60.15.0", {"start": v(-43.1, -7.51) * mm, "end": v(-46.98, -25.7) * mm});
            skLineSegment(sketch, "E60.15.1", {"start": v(-46.98, -25.7) * mm, "end": v(-44.84, -26.07) * mm, "construction": true});
            skLineSegment(sketch, "E60.15.2", {"start": v(-44.84, -26.07) * mm, "end": v(-42.47, -7.62) * mm});
            skLineSegment(sketch, "E60.15.3", {"start": v(-42.7, -23.05) * mm, "end": v(-41.89, -7.67) * mm});
            skLineSegment(sketch, "E60.15.4", {"start": v(-40.04, -23.04) * mm, "end": v(-42.7, -23.05) * mm});
            skLineSegment(sketch, "E60.15.5", {"start": v(-40.04, -23.04) * mm, "end": v(-41, -7.67) * mm});
            skLineSegment(sketch, "E60.16.0", {"start": v(-40.43, -7.6) * mm, "end": v(-37.86, -26.03) * mm});
            skLineSegment(sketch, "E60.16.1", {"start": v(-37.86, -26.03) * mm, "end": v(-35.73, -25.64) * mm, "construction": true});
            skLineSegment(sketch, "E60.16.2", {"start": v(-35.73, -25.64) * mm, "end": v(-39.8, -7.5) * mm});
            skLineSegment(sketch, "E60.16.3", {"start": v(-34.74, -22.08) * mm, "end": v(-39.24, -7.35) * mm});
            skLineSegment(sketch, "E60.16.4", {"start": v(-32.24, -21.15) * mm, "end": v(-34.74, -22.08) * mm});
            skLineSegment(sketch, "E60.16.5", {"start": v(-32.24, -21.15) * mm, "end": v(-38.41, -7.04) * mm});
            skLineSegment(sketch, "E60.17.0", {"start": v(-37.89, -6.79) * mm, "end": v(-29.18, -23.22) * mm});
            skLineSegment(sketch, "E60.17.1", {"start": v(-29.18, -23.22) * mm, "end": v(-27.3, -22.13) * mm, "construction": true});
            skLineSegment(sketch, "E60.17.2", {"start": v(-27.3, -22.13) * mm, "end": v(-37.34, -6.47) * mm});
            skLineSegment(sketch, "E60.17.3", {"start": v(-27.6, -18.44) * mm, "end": v(-36.86, -6.14) * mm});
            skLineSegment(sketch, "E60.17.4", {"start": v(-25.57, -16.72) * mm, "end": v(-27.6, -18.44) * mm});
            skLineSegment(sketch, "E60.17.5", {"start": v(-25.57, -16.72) * mm, "end": v(-36.19, -5.56) * mm});
            skArc(sketch, "E61", {"start": v(-45.09, 6.79) * mm, "mid": v(-45.36, 6.63) * mm, "end": v(-45.63, 6.47) * mm});
            skArc(sketch, "E62.trimOffspring", {"start": v(-46.11, 6.14) * mm, "mid": v(-46.46, 5.86) * mm, "end": v(-46.79, 5.56) * mm});
            skArc(sketch, "E63.trimOffspring", {"start": v(-47.2, 5.15) * mm, "mid": v(-47.4, 4.9) * mm, "end": v(-47.6, 4.66) * mm});
            skArc(sketch, "E64.trimOffspring", {"start": v(-47.93, 4.18) * mm, "mid": v(-48.16, 3.8) * mm, "end": v(-48.37, 3.42) * mm});
            skArc(sketch, "E65.trimOffspring", {"start": v(-48.6, 2.89) * mm, "mid": v(-48.72, 2.6) * mm, "end": v(-48.82, 2.29) * mm});
            skArc(sketch, "E66.trimOffspring", {"start": v(-48.97, 1.73) * mm, "mid": v(-49.06, 1.3) * mm, "end": v(-49.12, 0.86) * mm});
            skArc(sketch, "E67.trimOffspring", {"start": v(-43.73, 7.35) * mm, "mid": v(-44.15, 7.2) * mm, "end": v(-44.56, 7.04) * mm});
            skArc(sketch, "E68.trimOffspring", {"start": v(-42.55, 7.6) * mm, "mid": v(-42.86, 7.56) * mm, "end": v(-43.17, 7.5) * mm});
            skArc(sketch, "E69.trimOffspring", {"start": v(-41.08, 7.67) * mm, "mid": v(-41.53, 7.68) * mm, "end": v(-41.97, 7.67) * mm});
            skArc(sketch, "E70.trimOffspring", {"start": v(-39.88, 7.51) * mm, "mid": v(-40.2, 7.57) * mm, "end": v(-40.5, 7.62) * mm});
            skArc(sketch, "E71.trimOffspring", {"start": v(-38.48, 7.07) * mm, "mid": v(-38.9, 7.23) * mm, "end": v(-39.32, 7.37) * mm});
            skArc(sketch, "E72.trimOffspring", {"start": v(-37.4, 6.51) * mm, "mid": v(-37.68, 6.67) * mm, "end": v(-37.96, 6.83) * mm});
            skArc(sketch, "E73.trimOffspring", {"start": v(-36.25, 5.62) * mm, "mid": v(-36.58, 5.91) * mm, "end": v(-36.93, 6.18) * mm});
            skArc(sketch, "E74.trimOffspring", {"start": v(-35.43, 4.72) * mm, "mid": v(-35.63, 4.97) * mm, "end": v(-35.84, 5.2) * mm});
            skArc(sketch, "E75.trimOffspring", {"start": v(-34.64, 3.49) * mm, "mid": v(-34.85, 3.88) * mm, "end": v(-35.09, 4.25) * mm});
            skArc(sketch, "E76.trimOffspring", {"start": v(-34.18, 2.37) * mm, "mid": v(-34.28, 2.67) * mm, "end": v(-34.4, 2.96) * mm});
            skArc(sketch, "E77.trimOffspring", {"start": v(-33.86, 0.94) * mm, "mid": v(-33.93, 1.37) * mm, "end": v(-34.02, 1.8) * mm});
            skArc(sketch, "E78.trimOffspring", {"start": v(-33.8, -0.28) * mm, "mid": v(-33.8, 0.04) * mm, "end": v(-33.81, 0.36) * mm});
            skArc(sketch, "E79.trimOffspring", {"start": v(-49.11, -0.94) * mm, "mid": v(-48.91, -1.97) * mm, "end": v(-48.58, -2.96) * mm});
            skArc(sketch, "E80.trimOffspring", {"start": v(-48.33, -3.49) * mm, "mid": v(-48.12, -3.88) * mm, "end": v(-47.89, -4.25) * mm});
            skArc(sketch, "E81.trimOffspring", {"start": v(-47.55, -4.72) * mm, "mid": v(-47.35, -4.97) * mm, "end": v(-47.14, -5.2) * mm});
            skArc(sketch, "E82.trimOffspring", {"start": v(-46.73, -5.62) * mm, "mid": v(-46.4, -5.91) * mm, "end": v(-46.05, -6.18) * mm});
            skArc(sketch, "E83.trimOffspring", {"start": v(-45.57, -6.51) * mm, "mid": v(-45.3, -6.67) * mm, "end": v(-45.01, -6.83) * mm});
            skArc(sketch, "E84.trimOffspring", {"start": v(-44.49, -7.07) * mm, "mid": v(-44.08, -7.23) * mm, "end": v(-43.66, -7.37) * mm});
            skArc(sketch, "E85.trimOffspring", {"start": v(-43.1, -7.51) * mm, "mid": v(-42.78, -7.57) * mm, "end": v(-42.47, -7.62) * mm});
            skArc(sketch, "E86.trimOffspring", {"start": v(-41.89, -7.67) * mm, "mid": v(-41.45, -7.68) * mm, "end": v(-41, -7.67) * mm});
            skArc(sketch, "E87.trimOffspring", {"start": v(-40.43, -7.6) * mm, "mid": v(-40.11, -7.56) * mm, "end": v(-39.8, -7.5) * mm});
            skArc(sketch, "E88.trimOffspring", {"start": v(-39.24, -7.35) * mm, "mid": v(-38.82, -7.2) * mm, "end": v(-38.41, -7.04) * mm});
            skArc(sketch, "E89.trimOffspring", {"start": v(-37.89, -6.79) * mm, "mid": v(-37.61, -6.63) * mm, "end": v(-37.34, -6.47) * mm});
            skArc(sketch, "E90.trimOffspring", {"start": v(-36.86, -6.14) * mm, "mid": v(-36.52, -5.86) * mm, "end": v(-36.19, -5.56) * mm});
            skArc(sketch, "E91.trimOffspring", {"start": v(-35.78, -5.15) * mm, "mid": v(-35.58, -4.9) * mm, "end": v(-35.38, -4.66) * mm});
            skArc(sketch, "E92.trimOffspring", {"start": v(-35.04, -4.18) * mm, "mid": v(-34.81, -3.8) * mm, "end": v(-34.6, -3.42) * mm});
            skArc(sketch, "E93.trimOffspring", {"start": v(-34.37, -2.89) * mm, "mid": v(-34.27, -2.64) * mm, "end": v(-34.18, -2.38) * mm});
            skLineSegment(sketch, "E94", {"start": v(-19.45, -6.88) * mm, "end": v(-34.18, -2.38) * mm});
            skArc(sketch, "E95.trimOffspring", {"start": v(-34, -1.73) * mm, "mid": v(-33.91, -1.3) * mm, "end": v(-33.85, -0.86) * mm});
            skLineSegment(sketch, "E96", {"start": v(-62.22, -16.16) * mm, "end": v(-60.81, -17.81) * mm});
            skLineSegment(sketch, "E97", {"start": v(-65.74, -10.13) * mm, "end": v(-66.5, -8.1) * mm});
            skLineSegment(sketch, "E98", {"start": v(-67.74, -1.22) * mm, "end": v(-67.75, 0.95) * mm});
            skLineSegment(sketch, "E99", {"start": v(-66.57, 7.83) * mm, "end": v(-65.84, 9.87) * mm});
            skLineSegment(sketch, "E100", {"start": v(-37.86, -26.03) * mm, "end": v(-35.73, -25.64) * mm});
            skLineSegment(sketch, "E101", {"start": v(-29.18, -23.22) * mm, "end": v(-27.3, -22.13) * mm});
            skLineSegment(sketch, "E102", {"start": v(-21.98, -17.6) * mm, "end": v(-20.6, -15.94) * mm});
            skLineSegment(sketch, "E103", {"start": v(-46.98, -25.7) * mm, "end": v(-44.84, -26.07) * mm});
            skLineSegment(sketch, "E104", {"start": v(-53.56, -23.35) * mm, "end": v(-55.44, -22.27) * mm});
            skLineSegment(sketch, "E105", {"start": v(-62.38, 15.94) * mm, "end": v(-61, 17.6) * mm});
            skLineSegment(sketch, "E106", {"start": v(-55.67, 22.13) * mm, "end": v(-53.8, 23.22) * mm});
            skLineSegment(sketch, "E107", {"start": v(-47.25, 25.64) * mm, "end": v(-45.11, 26.03) * mm});
            skLineSegment(sketch, "E108", {"start": v(-38.13, 26.07) * mm, "end": v(-36, 25.7) * mm});
            skLineSegment(sketch, "E109", {"start": v(-29.42, 23.35) * mm, "end": v(-27.53, 22.27) * mm});
            skLineSegment(sketch, "E110", {"start": v(-22.16, 17.81) * mm, "end": v(-20.76, 16.16) * mm});
            skLineSegment(sketch, "E111", {"start": v(-17.23, 10.13) * mm, "end": v(-16.48, 8.1) * mm});
            skLineSegment(sketch, "E112", {"start": v(-15.23, 1.22) * mm, "end": v(-15.22, -0.95) * mm});
            skLineSegment(sketch, "E113", {"start": v(-16.4, -7.83) * mm, "end": v(-17.13, -9.87) * mm});
            skLineSegment(sketch, "E114", {"start": v(-49.16, -0.36) * mm, "end": v(-49.17, 0.28) * mm});
            skSolve(sketch);
        }
        {
            var Q0;
            Q0=qSketchRegion(id+"F9",true);
            extrude(context, id + "F10", {"entities" : qUnion([Q0]), "operationType" : NewBodyOperationType.REMOVE, "depth" : 4.5 * mm});
        }
        {
            var Q0;
            Q0=makeQuery(id+"F0.imprint","IMPRINT",FACE,{"disambiguationData":[TD([[makeQuery(id+"F0.imprint","IMPRINT",EDGE,{"derivedFrom":sQuery(id+"F0.wireOp",EDGE,"E0")}),-1.0]])]});
            var sketch = newSketch(context, id + "F11", { "sketchPlane" : qUnion([Q0])});
            skCircle(sketch, "E115", {"center": v(-41.49, 0) * mm, "radius": 5.37 * mm});
            skCircle(sketch, "E116", {"center": v(-41.49, 0) * mm, "radius": 7.09 * mm});
            skLineSegment(sketch, "E117.bottom", {"start": v(-41.49, 0) * mm, "end": v(-41.49, 0) * mm});
            skSolve(sketch);
        }
        {
            var Q0;
            Q0=qSketchRegion(id+"F11",true);
            var Q1;
            Q1=makeQuery(id+"F10.boolean.opBoolean","COPY",FACE,{"derivedFrom":makeQuery(id+"F10.opExtrude","CAP_FACE",FACE,{"disambiguationData":[OSD([sQuery(id+"F9.wireOp",EDGE,"E60.11.3"),sQuery(id+"F9.wireOp",EDGE,"E60.11.4"),sQuery(id+"F9.wireOp",EDGE,"E60.11.5"),sQuery(id+"F9.wireOp",EDGE,"E79.trimOffspring")])],"isStart":false})});
            extrude(context, id + "F12", {"entities" : qUnion([Q0]), "operationType" : NewBodyOperationType.REMOVE, "endBound" : BoundingType.UP_TO_SURFACE, "endBoundEntityFace" : qUnion([Q1]), "depth" : 25 * mm});
        }
        {
            var Q0;
            {var subQ0=sQuery(id+"F0.wireOp",EDGE,"E36");var subQ1=sQuery(id+"F0.wireOp",EDGE,"E35");var subQ2=sQuery(id+"F0.wireOp",EDGE,"E34");var subQ3=sQuery(id+"F0.wireOp",EDGE,"E33");var subQ4=sQuery(id+"F0.wireOp",EDGE,"E32");var subQ5=sQuery(id+"F0.wireOp",EDGE,"E31");var subQ6=sQuery(id+"F0.wireOp",EDGE,"E30");var subQ7=sQuery(id+"F0.wireOp",EDGE,"E29");var subQ8=sQuery(id+"F0.wireOp",EDGE,"E28");var subQ9=sQuery(id+"F0.wireOp",EDGE,"E27");var subQ10=sQuery(id+"F0.wireOp",EDGE,"E26");var subQ11=sQuery(id+"F0.wireOp",EDGE,"E25");var subQ12=sQuery(id+"F0.wireOp",EDGE,"E24");var subQ13=sQuery(id+"F0.wireOp",EDGE,"E23");var subQ14=sQuery(id+"F0.wireOp",EDGE,"E22");var subQ15=sQuery(id+"F0.wireOp",EDGE,"E21");var subQ16=sQuery(id+"F0.wireOp",EDGE,"E20");var subQ17=sQuery(id+"F0.wireOp",EDGE,"E19");var subQ18=sQuery(id+"F0.wireOp",EDGE,"E18");var subQ19=sQuery(id+"F0.wireOp",EDGE,"E17");var subQ20=sQuery(id+"F0.wireOp",EDGE,"E16");var subQ21=sQuery(id+"F0.wireOp",EDGE,"E15");var subQ22=sQuery(id+"F0.wireOp",EDGE,"E14");var subQ23=sQuery(id+"F0.wireOp",EDGE,"E13");var subQ24=sQuery(id+"F0.wireOp",EDGE,"E12");var subQ25=sQuery(id+"F0.wireOp",EDGE,"E11");var subQ26=sQuery(id+"F0.wireOp",EDGE,"E10");var subQ27=sQuery(id+"F0.wireOp",EDGE,"E9");var subQ28=sQuery(id+"F0.wireOp",EDGE,"E8");var subQ29=sQuery(id+"F0.wireOp",EDGE,"E7");var subQ30=sQuery(id+"F0.wireOp",EDGE,"E6");var subQ31=sQuery(id+"F0.wireOp",EDGE,"E5");var subQ32=sQuery(id+"F0.wireOp",EDGE,"E4");var subQ33=sQuery(id+"F0.wireOp",EDGE,"E3");var subQ34=sQuery(id+"F0.wireOp",EDGE,"E1");var subQ35=sQuery(id+"F0.wireOp",EDGE,"E0");Q0=makeQuery(id+"F5.boolean.opBoolean","MERGE",FACE,{"derivedFrom":[makeQuery(id+"F1.opExtrude","CAP_FACE",FACE,{"disambiguationData":[OSD([subQ35,subQ34,subQ33,subQ32,subQ31,subQ30,subQ29,subQ28,subQ27,subQ26,subQ25,subQ24,subQ23,subQ22,subQ21,subQ20,subQ19,subQ18,subQ17,subQ16,subQ15,subQ14,subQ13,subQ12,subQ11,subQ10,subQ9,subQ8,subQ7,subQ6,subQ5,subQ4,subQ3,subQ2,subQ1,subQ0])],"isStart":false}),makeQuery(id+"F5.opExtrude","CAP_FACE",FACE,{"disambiguationData":[OSD([subQ35,subQ34,subQ33,subQ32,subQ31,subQ30,subQ29,subQ28,subQ27,subQ26,subQ25,subQ24,subQ23,subQ22,subQ21,subQ20,subQ19,subQ18,subQ17,subQ16,subQ15,subQ14,subQ13,subQ12,subQ11,subQ10,subQ9,subQ8,subQ7,subQ6,subQ5,subQ4,subQ3,subQ2,subQ1,subQ0])],"isStart":false})]});}
            var sketch = newSketch(context, id + "F13", { "sketchPlane" : qUnion([Q0])});
            skText(sketch, "E118", { "text": "Jonathan\n  Aguirre", "fontName": "OpenSans-Bold.ttf"});
            const initialGuessF13  = {"E118": [-0.06386, 0.00224, 1, 0, 0.0071]};
            skSetInitialGuess(sketch, initialGuessF13);
            skSolve(sketch);
        }
        {
            var Q0;
            Q0=qSketchRegion(id+"F13",true);
            extrude(context, id + "F14", {"entities" : qUnion([Q0]), "operationType" : NewBodyOperationType.ADD, "depth" : 3 * mm});
        }
    });
